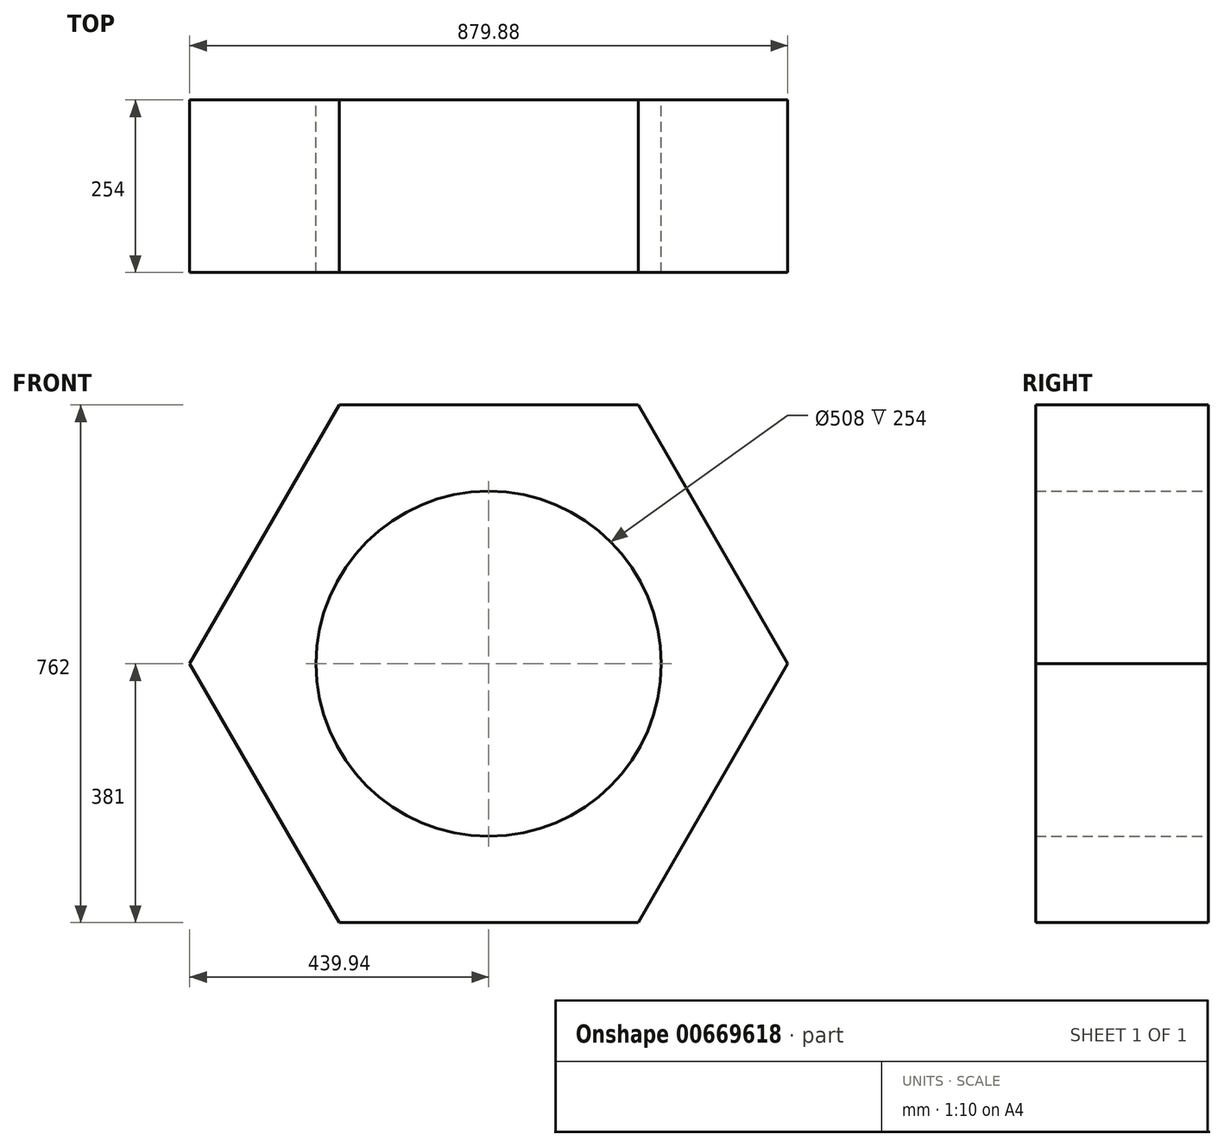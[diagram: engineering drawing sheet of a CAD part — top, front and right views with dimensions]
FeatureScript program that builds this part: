
annotation { "Feature Type Name" : "Feature", "Feature Type Description" : "" }
export const myFeature = defineFeature(function(context is Context, id is Id, definition is map)
    precondition{}
    {
        {
            var Q0;
            Q0=qCreatedBy(makeId("Front.planeOp"),FACE);
            var sketch = newSketch(context, id + "F0", { "sketchPlane" : qUnion([Q0])});
            skCircle(sketch, "E0.cCircle", {"center": v(0, 0) * mm, "radius": 381 * mm, "construction": true});
            skLineSegment(sketch, "E0.0", {"start": v(-219.97, 381) * mm, "end": v(219.97, 381) * mm});
            skLineSegment(sketch, "E0.1", {"start": v(219.97, 381) * mm, "end": v(439.94, 0) * mm});
            skLineSegment(sketch, "E0.2", {"start": v(439.94, 0) * mm, "end": v(219.97, -381) * mm});
            skLineSegment(sketch, "E0.3", {"start": v(219.97, -381) * mm, "end": v(-219.97, -381) * mm});
            skLineSegment(sketch, "E0.4", {"start": v(-219.97, -381) * mm, "end": v(-439.94, 0) * mm});
            skLineSegment(sketch, "E0.5", {"start": v(-439.94, 0) * mm, "end": v(-219.97, 381) * mm});
            skPoint(sketch, "E0.0.midPoint", {"position": v(0, 381) * mm});
            skCircle(sketch, "E1", {"center": v(0, 0) * mm, "radius": 254 * mm});
            skSolve(sketch);
        }
        {
            var Q0;
            Q0=makeQuery(id+"F0.imprint","IMPRINT",FACE,{"disambiguationData":[TD([[makeQuery(id+"F0.imprint","IMPRINT",EDGE,{"derivedFrom":sQuery(id+"F0.wireOp",EDGE,"E0.0")}),-1.0]])]});
            extrude(context, id + "F1", {"entities" : qUnion([Q0]), "depth" : 254 * mm, "offsetDistance" : 25.4 * mm});
        }
    });
